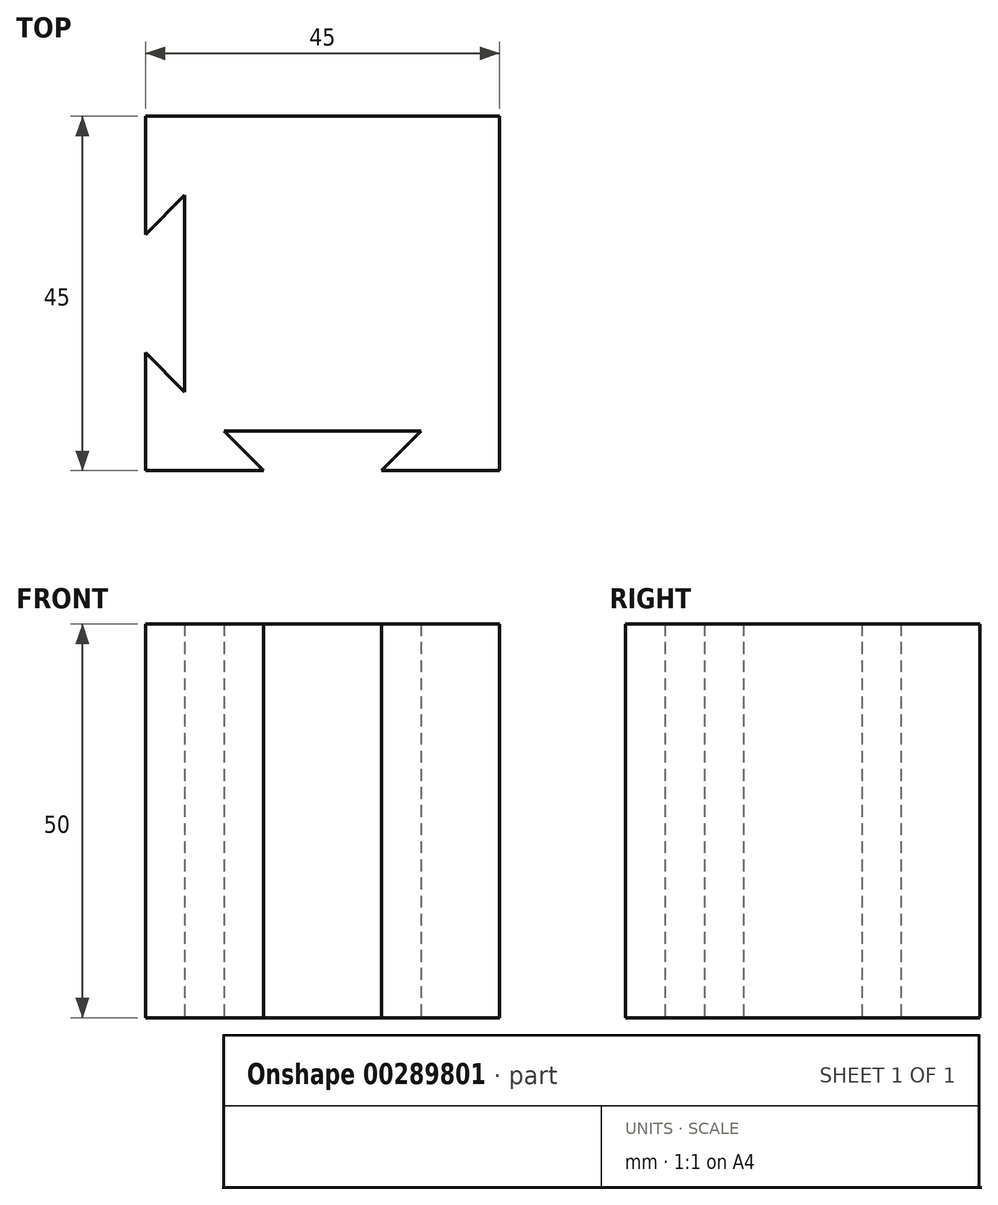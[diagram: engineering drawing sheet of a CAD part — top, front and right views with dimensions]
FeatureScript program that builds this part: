
annotation { "Feature Type Name" : "Feature", "Feature Type Description" : "" }
export const myFeature = defineFeature(function(context is Context, id is Id, definition is map)
    precondition{}
    {
        {
            var Q0;
            Q0=qCreatedBy(makeId("Top.planeOp"),FACE);
            var sketch = newSketch(context, id + "F0", { "sketchPlane" : qUnion([Q0])});
            skLineSegment(sketch, "E0.bottom", {"start": v(-21.13, 19.28) * mm, "end": v(-6.13, 19.28) * mm});
            skLineSegment(sketch, "E0.top", {"start": v(-21.13, -25.72) * mm, "end": v(-6.13, -25.72) * mm});
            skLineSegment(sketch, "E0.left", {"start": v(-21.13, 19.28) * mm, "end": v(-21.13, 4.28) * mm});
            skLineSegment(sketch, "E0.right", {"start": v(23.87, 19.28) * mm, "end": v(23.87, 4.28) * mm});
            skLineSegment(sketch, "E1.1", {"start": v(-16.13, 9.28) * mm, "end": v(-16.13, -15.72) * mm});
            skLineSegment(sketch, "E1.2", {"start": v(-11.13, -20.72) * mm, "end": v(13.87, -20.72) * mm});
            skLineSegment(sketch, "E2", {"start": v(-21.13, 4.28) * mm, "end": v(-16.13, 9.28) * mm});
            skLineSegment(sketch, "E3", {"start": v(-6.13, -25.72) * mm, "end": v(-11.13, -20.72) * mm});
            skLineSegment(sketch, "E4.trimOffspring", {"start": v(8.87, 19.28) * mm, "end": v(23.87, 19.28) * mm});
            skPoint(sketch, "E5.orphan", {"position": v(1.37, 19.28) * mm});
            skLineSegment(sketch, "E6.trimOffspring", {"start": v(-21.13, -10.72) * mm, "end": v(-21.13, -25.72) * mm});
            skPoint(sketch, "E7.orphan", {"position": v(-21.13, -3.22) * mm});
            skLineSegment(sketch, "E8.trimOffspring", {"start": v(-16.13, -15.72) * mm, "end": v(-21.13, -10.72) * mm});
            skLineSegment(sketch, "E9.trimOffspring", {"start": v(23.87, -10.72) * mm, "end": v(23.87, -25.72) * mm});
            skPoint(sketch, "E10.orphan", {"position": v(23.87, -3.22) * mm});
            skLineSegment(sketch, "E11.trimOffspring", {"start": v(8.87, -25.72) * mm, "end": v(23.87, -25.72) * mm});
            skPoint(sketch, "E12.orphan", {"position": v(1.37, -25.72) * mm});
            skLineSegment(sketch, "E13.trimOffspring", {"start": v(13.87, -20.72) * mm, "end": v(8.87, -25.72) * mm});
            skLineSegment(sketch, "E14.bottom", {"start": v(-21.13, 19.28) * mm, "end": v(23.87, 19.28) * mm});
            skLineSegment(sketch, "E14.right", {"start": v(23.87, 19.28) * mm, "end": v(23.87, -25.72) * mm});
            skSolve(sketch);
        }
        {
            var Q0;
            Q0=makeQuery(id+"F0.imprint","IMPRINT",FACE,{"disambiguationData":[TD([[makeQuery(id+"F0.imprint","IMPRINT",EDGE,{"derivedFrom":sQuery(id+"F0.wireOp",EDGE,"E1.0")}),-1.0]])]});
            var Q1;
            Q1=makeQuery(id+"F0.imprint","IMPRINT",FACE,{"disambiguationData":[TD([[makeQuery(id+"F0.imprint","IMPRINT",EDGE,{"derivedFrom":sQuery(id+"F0.wireOp",EDGE,"E1.1")}),1.0]])]});
            extrude(context, id + "F1", {"entities" : qUnion([Q0, Q1]), "depth" : 50 * mm});
        }
    });
